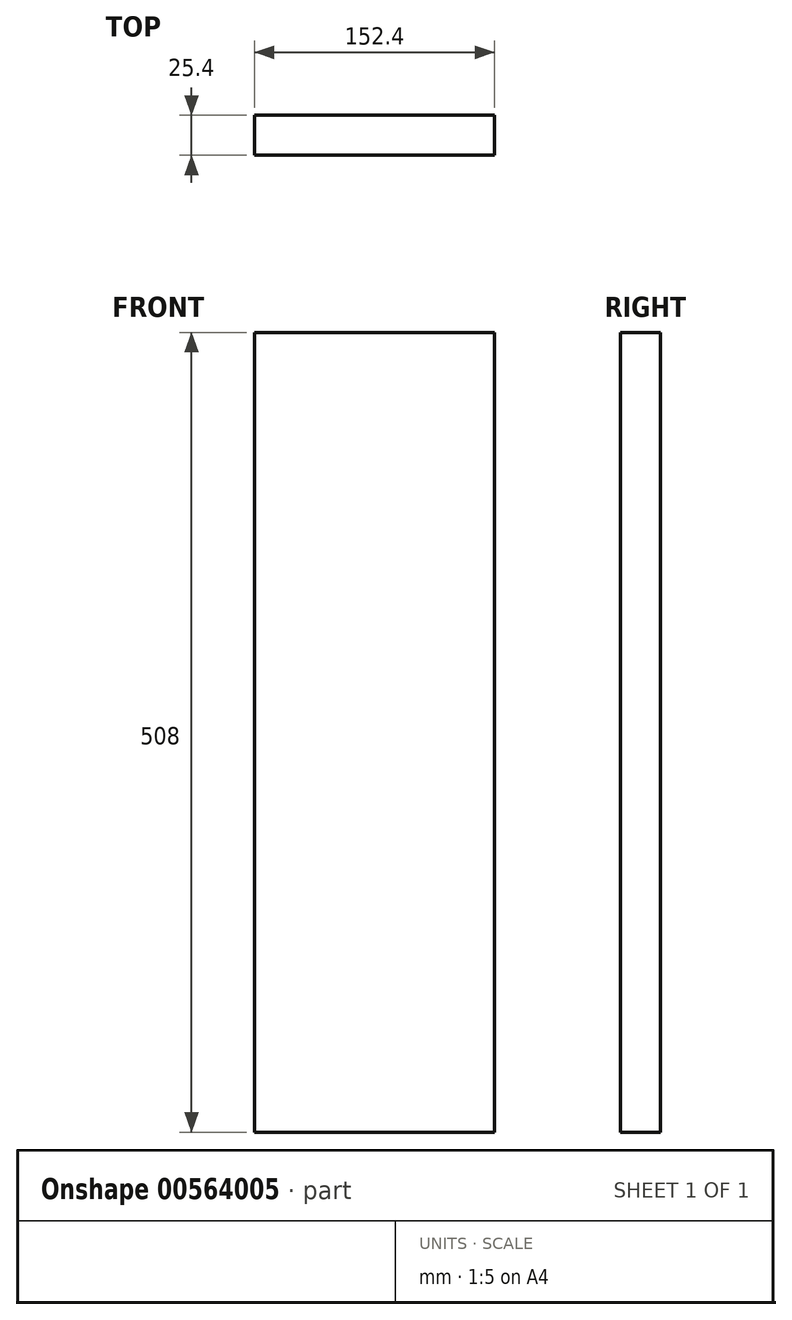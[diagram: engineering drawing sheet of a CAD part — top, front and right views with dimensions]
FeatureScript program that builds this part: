
annotation { "Feature Type Name" : "Feature", "Feature Type Description" : "" }
export const myFeature = defineFeature(function(context is Context, id is Id, definition is map)
    precondition{}
    {
        {
            var Q0;
            Q0=qCreatedBy(makeId("Front.planeOp"),FACE);
            var sketch = newSketch(context, id + "F0", { "sketchPlane" : qUnion([Q0])});
            skLineSegment(sketch, "E0.bottom", {"start": v(76.2, -254) * mm, "end": v(-76.2, -254) * mm});
            skLineSegment(sketch, "E0.top", {"start": v(76.2, 254) * mm, "end": v(-76.2, 254) * mm});
            skLineSegment(sketch, "E0.left", {"start": v(76.2, -254) * mm, "end": v(76.2, 254) * mm});
            skLineSegment(sketch, "E0.right", {"start": v(-76.2, -254) * mm, "end": v(-76.2, 254) * mm});
            skPoint(sketch, "E0.middle", {"position": v(0, 0) * mm});
            skSolve(sketch);
        }
        {
            var Q0;
            Q0=makeQuery(id+"F0.imprint","IMPRINT",FACE,{"disambiguationData":[TD([[makeQuery(id+"F0.imprint","IMPRINT",EDGE,{"derivedFrom":sQuery(id+"F0.wireOp",EDGE,"E0.bottom")}),-1.0]])]});
            extrude(context, id + "F1", {"entities" : qUnion([Q0]), "oppositeDirection" : true, "depth" : 25.4 * mm, "offsetDistance" : 25.4 * mm});
        }
    });
